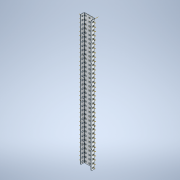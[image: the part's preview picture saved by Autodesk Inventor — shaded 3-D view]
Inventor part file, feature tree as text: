
AUTODESK INVENTOR PART (.ipt)
format: ipt  version: 2020 (Build 240168000, 168)  size: 1,433,088 bytes
history: native  units: in
note: dims shown in document units (in); Inventor stores cm internally (conversion verified against a paired STEP export)
features: other x175, plane x6, pattern_linear x3, sheet_metal_op x1
ambient origin geometry x8: Origin, YZ Plane, XZ Plane, XY Plane, X Axis, Y Axis, Z Axis, Center Point
bodies: Solid1 (feature_tree)
feature tree (185):
  other  "Work Axis106"
  pattern_linear  "Rectangular Pattern2"  Count1=35 Spacing1=0.5in
  other  "Work Axis211"
  pattern_linear  "Rectangular Pattern3"  Count1=3 Spacing1=0.5in
  other  "Work Axis246"
  pattern_linear  "Rectangular Pattern4"  Count1=35 Spacing1=0.5in
  plane  "Work Plane3"
  plane  "Work Plane4"
  other  "Work Axis107"
  other  "Work Axis108"
  other  "Work Axis109"
  other  "Work Axis110"
  other  "Work Axis111"
  other  "Work Axis112"
  other  "Work Axis113"
  other  "Work Axis114"
  other  "Work Axis115"
  other  "Work Axis116"
  other  "Work Axis117"
  other  "Work Axis118"
  other  "Work Axis119"
  other  "Work Axis120"
  other  "Work Axis121"
  other  "Work Axis122"
  other  "Work Axis123"
  other  "Work Axis124"
  other  "Work Axis125"
  other  "Work Axis126"
  other  "Work Axis127"
  other  "Work Axis128"
  other  "Work Axis129"
  other  "Work Axis130"
  other  "Work Axis131"
  other  "Work Axis132"
  other  "Work Axis133"
  other  "Work Axis134"
  other  "Work Axis135"
  other  "Work Axis136"
  other  "Work Axis137"
  other  "Work Axis138"
  other  "Work Axis139"
  other  "Work Axis140"
  other  "Work Axis141"
  other  "Work Axis142"
  other  "Work Axis143"
  other  "Work Axis144"
  other  "Work Axis145"
  other  "Work Axis146"
  other  "Work Axis147"
  other  "Work Axis148"
  other  "Work Axis149"
  other  "Work Axis150"
  other  "Work Axis151"
  other  "Work Axis152"
  other  "Work Axis153"
  other  "Work Axis154"
  other  "Work Axis155"
  other  "Work Axis156"
  other  "Work Axis157"
  other  "Work Axis158"
  other  "Work Axis159"
  other  "Work Axis160"
  other  "Work Axis161"
  other  "Work Axis162"
  other  "Work Axis163"
  other  "Work Axis164"
  other  "Work Axis165"
  other  "Work Axis166"
  other  "Work Axis167"
  other  "Work Axis168"
  other  "Work Axis169"
  other  "Work Axis170"
  other  "Work Axis171"
  other  "Work Axis172"
  other  "Work Axis173"
  other  "Work Axis174"
  other  "Work Axis175"
  other  "Work Axis176"
  other  "Work Axis177"
  other  "Work Axis178"
  other  "Work Axis179"
  other  "Work Axis180"
  other  "Work Axis181"
  other  "Work Axis182"
  other  "Work Axis183"
  other  "Work Axis184"
  other  "Work Axis185"
  other  "Work Axis186"
  other  "Work Axis187"
  other  "Work Axis188"
  other  "Work Axis189"
  other  "Work Axis190"
  other  "Work Axis191"
  other  "Work Axis192"
  other  "Work Axis193"
  other  "Work Axis194"
  other  "Work Axis195"
  other  "Work Axis196"
  other  "Work Axis197"
  other  "Work Axis198"
  other  "Work Axis199"
  other  "Work Axis200"
  other  "Work Axis201"
  other  "Work Axis202"
  other  "Work Axis203"
  other  "Work Axis204"
  other  "Work Axis205"
  other  "Work Axis206"
  other  "Work Axis207"
  other  "Work Axis208"
  other  "Work Axis209"
  other  "Work Axis210"
  plane  "Work Plane5"
  plane  "Work Plane6"
  other  "Work Axis212"
  other  "Work Axis213"
  other  "Work Axis214"
  other  "Work Axis215"
  other  "Work Axis216"
  other  "Work Axis217"
  other  "Work Axis218"
  other  "Work Axis219"
  other  "Work Axis220"
  other  "Work Axis221"
  other  "Work Axis222"
  other  "Work Axis223"
  other  "Work Axis224"
  other  "Work Axis225"
  other  "Work Axis226"
  other  "Work Axis227"
  other  "Work Axis228"
  other  "Work Axis229"
  other  "Work Axis230"
  other  "Work Axis231"
  other  "Work Axis232"
  other  "Work Axis233"
  other  "Work Axis234"
  other  "Work Axis235"
  other  "Work Axis236"
  other  "Work Axis237"
  other  "Work Axis238"
  other  "Work Axis239"
  other  "Work Axis240"
  other  "Work Axis241"
  other  "Work Axis242"
  other  "Work Axis243"
  other  "Work Axis244"
  other  "Work Axis245"
  plane  "Work Plane7"
  plane  "Work Plane8"
  other  "Work Axis247"
  other  "Work Axis248"
  other  "Work Axis249"
  other  "Work Axis250"
  other  "Work Axis251"
  other  "Work Axis252"
  other  "Work Axis253"
  other  "Work Axis254"
  other  "Work Axis255"
  other  "Work Axis256"
  other  "Work Axis257"
  other  "Work Axis258"
  other  "Work Axis259"
  other  "Work Axis260"
  other  "Work Axis261"
  other  "Work Axis262"
  other  "Work Axis263"
  other  "Work Axis264"
  other  "Work Axis265"
  other  "Work Axis266"
  other  "Work Axis267"
  other  "Work Axis268"
  other  "Work Axis269"
  other  "Work Axis270"
  other  "Work Axis271"
  other  "Work Axis272"
  other  "Work Axis273"
  other  "Work Axis274"
  other  "Work Axis275"
  other  "Work Axis276"
  other  "Work Axis277"
  other  "Work Axis278"
  other  "Work Axis279"
  other  "Work Axis280"
  sheet_metal_op  "Fold1"
